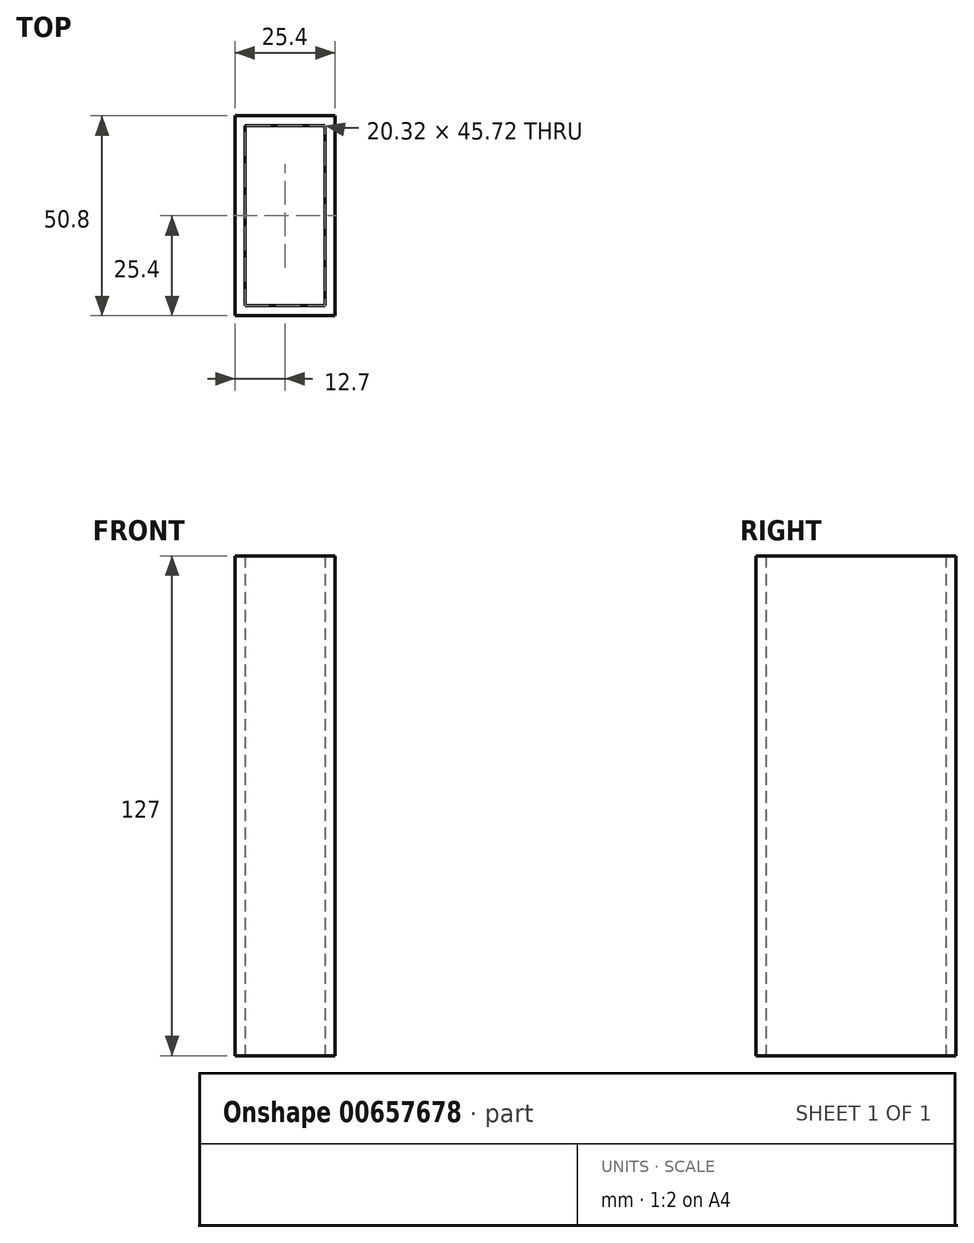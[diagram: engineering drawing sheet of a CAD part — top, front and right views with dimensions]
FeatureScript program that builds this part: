
annotation { "Feature Type Name" : "Feature", "Feature Type Description" : "" }
export const myFeature = defineFeature(function(context is Context, id is Id, definition is map)
    precondition{}
    {
        {
            var Q0;
            Q0=qCreatedBy(makeId("Top.planeOp"),FACE);
            var sketch = newSketch(context, id + "F0", { "sketchPlane" : qUnion([Q0])});
            skLineSegment(sketch, "E0.bottom", {"start": v(0, 0) * mm, "end": v(25.4, 0) * mm});
            skLineSegment(sketch, "E0.top", {"start": v(0, -50.8) * mm, "end": v(25.4, -50.8) * mm});
            skLineSegment(sketch, "E0.left", {"start": v(0, 0) * mm, "end": v(0, -50.8) * mm});
            skLineSegment(sketch, "E0.right", {"start": v(25.4, 0) * mm, "end": v(25.4, -50.8) * mm});
            skLineSegment(sketch, "E1.bottom", {"start": v(2.54, -48.26) * mm, "end": v(22.86, -48.26) * mm});
            skLineSegment(sketch, "E1.top", {"start": v(2.54, -2.54) * mm, "end": v(22.86, -2.54) * mm});
            skLineSegment(sketch, "E1.left", {"start": v(2.54, -48.26) * mm, "end": v(2.54, -2.54) * mm});
            skLineSegment(sketch, "E1.right", {"start": v(22.86, -48.26) * mm, "end": v(22.86, -2.54) * mm});
            skSolve(sketch);
        }
        {
            var Q0;
            Q0=makeQuery(id+"F0.imprint","IMPRINT",FACE,{"disambiguationData":[TD([[makeQuery(id+"F0.imprint","IMPRINT",EDGE,{"derivedFrom":sQuery(id+"F0.wireOp",EDGE,"E0.bottom")}),-1.0]])]});
            extrude(context, id + "F1", {"entities" : qUnion([Q0]), "depth" : 127 * mm, "offsetDistance" : 25.4 * mm});
        }
    });
